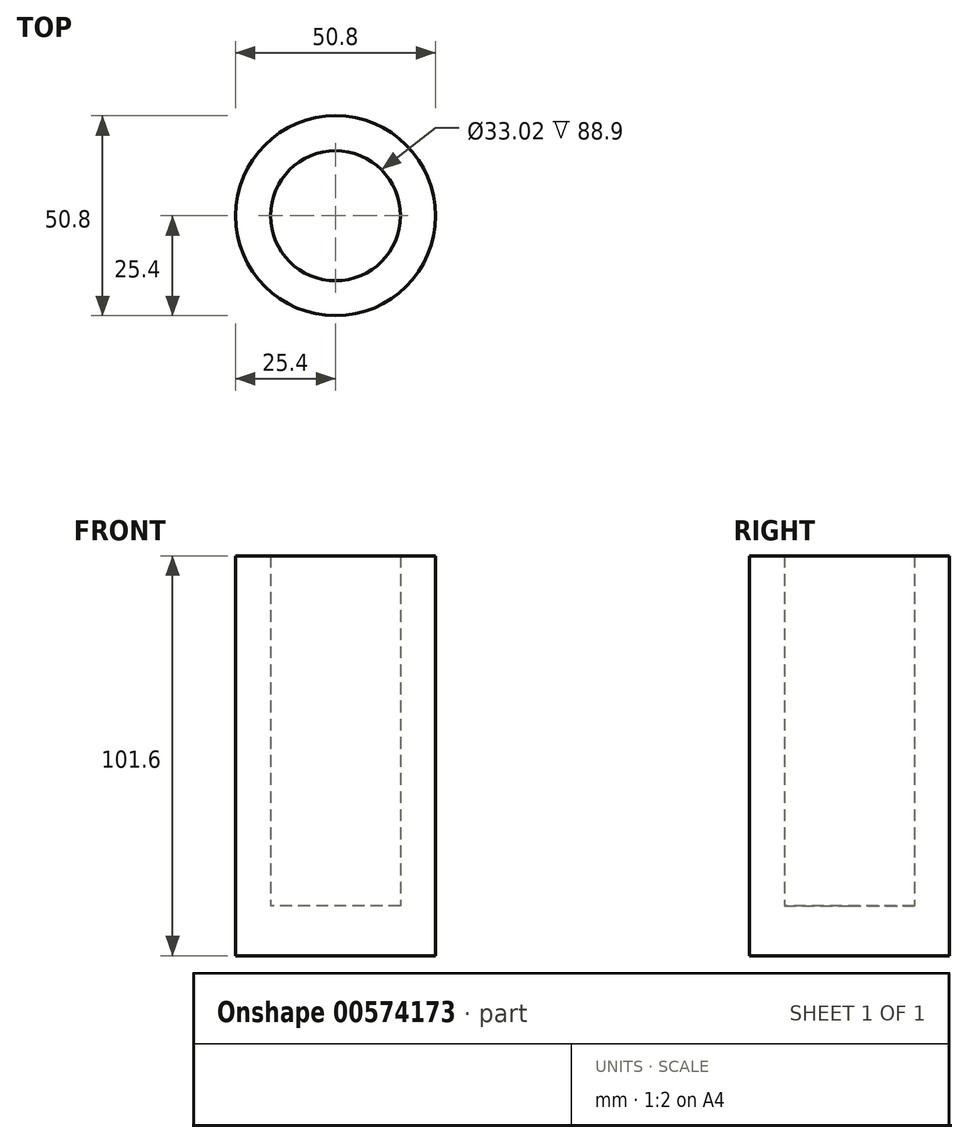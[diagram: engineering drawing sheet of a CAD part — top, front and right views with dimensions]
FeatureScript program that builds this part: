
annotation { "Feature Type Name" : "Feature", "Feature Type Description" : "" }
export const myFeature = defineFeature(function(context is Context, id is Id, definition is map)
    precondition{}
    {
        {
            var Q0;
            Q0=qCreatedBy(makeId("Top.planeOp"),FACE);
            var sketch = newSketch(context, id + "F0", { "sketchPlane" : qUnion([Q0])});
            skCircle(sketch, "E0", {"center": v(0, 0) * mm, "radius": 25.4 * mm});
            skCircle(sketch, "E1", {"center": v(0, 0) * mm, "radius": 16.51 * mm});
            skSolve(sketch);
        }
        {
            var Q0;
            Q0=makeQuery(id+"F0.imprint","IMPRINT",FACE,{"disambiguationData":[TD([[makeQuery(id+"F0.imprint","IMPRINT",EDGE,{"derivedFrom":sQuery(id+"F0.wireOp",EDGE,"E0")}),1.0]])]});
            extrude(context, id + "F1", {"entities" : qUnion([Q0]), "depth" : 101.6 * mm, "offsetDistance" : 25.4 * mm});
        }
        {
            var Q0;
            Q0=qCreatedBy(makeId("Top.planeOp"),FACE);
            var sketch = newSketch(context, id + "F2", { "sketchPlane" : qUnion([Q0])});
            skCircle(sketch, "E2", {"center": v(0, 0) * mm, "radius": 19.06 * mm});
            skSolve(sketch);
        }
        {
            var Q0;
            Q0 = qSketchRegion(id + "F2", true);
            extrude(context, id + "F3", {"entities" : qUnion([Q0]), "operationType" : NewBodyOperationType.ADD, "depth" : 12.7 * mm, "offsetDistance" : 25.4 * mm});
        }
    });
